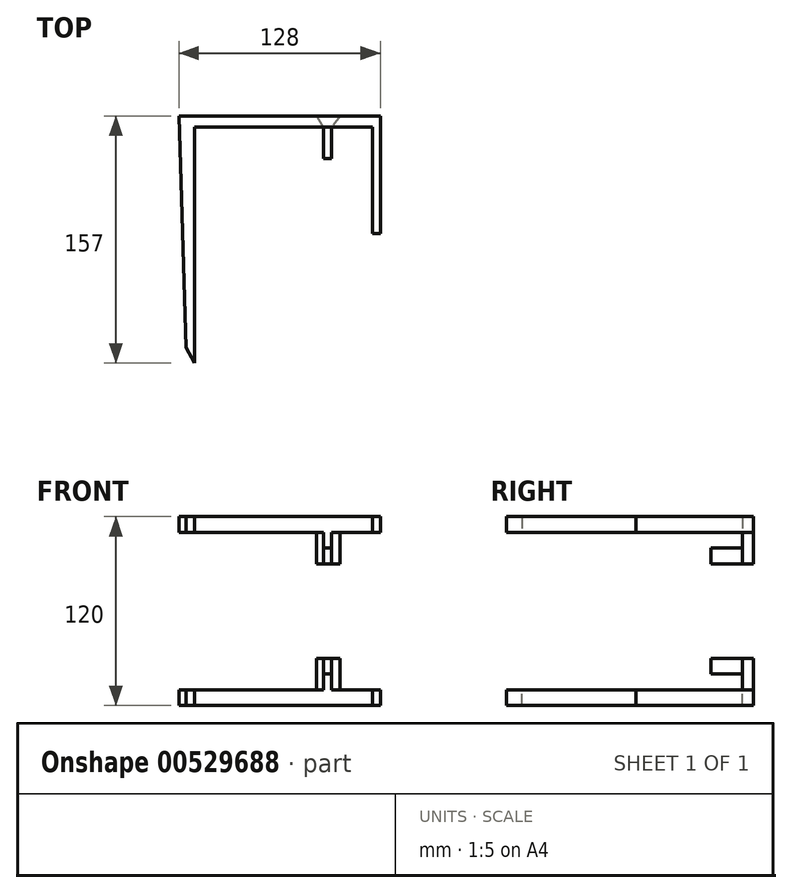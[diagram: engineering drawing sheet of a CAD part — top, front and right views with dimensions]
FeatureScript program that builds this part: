
annotation { "Feature Type Name" : "Feature", "Feature Type Description" : "" }
export const myFeature = defineFeature(function(context is Context, id is Id, definition is map)
    precondition{}
    {
        {
            var Q0;
            Q0=qCreatedBy(makeId("Top.planeOp"),FACE);
            var sketch = newSketch(context, id + "F0", { "sketchPlane" : qUnion([Q0])});
            skLineSegment(sketch, "E0", {"start": v(-97.85, -80.95) * mm, "end": v(-92.49, -90.95) * mm});
            skLineSegment(sketch, "E1", {"start": v(-92.49, -90.95) * mm, "end": v(-92.49, 59.05) * mm});
            skLineSegment(sketch, "E2", {"start": v(-92.49, 59.05) * mm, "end": v(20.51, 59.05) * mm});
            skLineSegment(sketch, "E3", {"start": v(20.51, 59.05) * mm, "end": v(20.51, -8.55) * mm});
            skLineSegment(sketch, "E4", {"start": v(20.51, -8.55) * mm, "end": v(25.51, -8.55) * mm});
            skLineSegment(sketch, "E5", {"start": v(25.51, -8.55) * mm, "end": v(25.51, 66.05) * mm});
            skLineSegment(sketch, "E6", {"start": v(25.51, 66.05) * mm, "end": v(-102.49, 66.05) * mm});
            skLineSegment(sketch, "E7", {"start": v(-102.49, 66.05) * mm, "end": v(-97.85, -80.95) * mm});
            skLineSegment(sketch, "E8.bottom", {"start": v(-10.49, 59.05) * mm, "end": v(-5.49, 59.05) * mm});
            skLineSegment(sketch, "E9", {"start": v(-16.3, 66.05) * mm, "end": v(0, 66.05) * mm});
            skSolve(sketch);
        }
        {
            var Q0;
            Q0=makeQuery(id+"F0.imprint","IMPRINT",FACE,{"disambiguationData":[TD([[makeQuery(id+"F0.imprint","IMPRINT",EDGE,{"derivedFrom":sQuery(id+"F0.wireOp",EDGE,"E0")}),1.0]])]});
            var Q1;
            {var subQ2=sQuery(id+"F0.wireOp",EDGE,"E3");Q1=makeQuery(id+"F0.imprint","IMPRINT",FACE,{"disambiguationData":[TD([[makeQuery(id+"F0.imprint","IMPRINT",EDGE,{"derivedFrom":subQ2}),1.0]])]});}
            var Q2;
            Q2=makeQuery(id+"F0.imprint","IMPRINT",FACE,{"disambiguationData":[TD([[makeQuery(id+"F0.imprint","IMPRINT",EDGE,{"derivedFrom":sQuery(id+"F0.wireOp",EDGE,"E8.bottom")}),1.0]])]});
            var Q3;
            Q3=sQuery(id+"F0.wireOp",EDGE,"E7");
            var Q4;
            Q4=sQuery(id+"F0.wireOp",EDGE,"E0");
            var Q5;
            Q5=sQuery(id+"F0.wireOp",EDGE,"E1");
            var Q6;
            Q6=sQuery(id+"F0.wireOp",EDGE,"E6");
            extrude(context, id + "F1", {"entities" : qUnion([Q0, Q1, Q2]), "surfaceEntities" : qUnion([Q3, Q4, Q5, Q6]), "oppositeDirection" : true, "depth" : 10 * mm});
        }
        {
            var Q0;
            Q0=makeQuery(id+"F1.opExtrude","CAP_FACE",FACE,{"disambiguationData":[OSD([sQuery(id+"F0.wireOp",EDGE,"E0"),sQuery(id+"F0.wireOp",EDGE,"E1"),sQuery(id+"F0.wireOp",EDGE,"E2"),sQuery(id+"F0.wireOp",EDGE,"E3"),sQuery(id+"F0.wireOp",EDGE,"E4"),sQuery(id+"F0.wireOp",EDGE,"E5"),sQuery(id+"F0.wireOp",EDGE,"E6"),sQuery(id+"F0.wireOp",EDGE,"E7"),sQuery(id+"F0.wireOp",EDGE,"E8.bottom"),sQuery(id+"F0.wireOp",EDGE,"E9")])],"isStart":true});
            var sketch = newSketch(context, id + "F2", { "sketchPlane" : qUnion([Q0])});
            skLineSegment(sketch, "E10", {"start": v(-5.49, 59.05) * mm, "end": v(-5.49, 29.05) * mm});
            skLineSegment(sketch, "E11", {"start": v(-5.49, 29.05) * mm, "end": v(-10.49, 29.05) * mm});
            skLineSegment(sketch, "E12", {"start": v(-10.49, 29.05) * mm, "end": v(-10.49, 59.05) * mm});
            skLineSegment(sketch, "E13", {"start": v(-10.49, 59.05) * mm, "end": v(-15, 66.05) * mm});
            skLineSegment(sketch, "E14", {"start": v(-15, 66.05) * mm, "end": v(0, 66.05) * mm});
            skLineSegment(sketch, "E15", {"start": v(0, 66.05) * mm, "end": v(-5.49, 59.05) * mm});
            skSolve(sketch);
        }
        {
            var Q0;
            {var subQ0=sQuery(id+"F2.wireOp",EDGE,"E13");Q0=makeQuery(id+"F2.imprint","IMPRINT",FACE,{"disambiguationData":[TD([[makeQuery(id+"F2.imprint","IMPRINT",EDGE,{"derivedFrom":subQ0}),-1.0]])]});}
            extrude(context, id + "F3", {"entities" : qUnion([Q0]), "operationType" : NewBodyOperationType.ADD, "depth" : 20 * mm});
        }
        {
            var Q0;
            {var subQ0=sQuery(id+"F0.wireOp",EDGE,"E8.bottom");var subQ1=sQuery(id+"F0.wireOp",EDGE,"E2");Q0=makeQuery(id+"F3.boolean.opBoolean","MERGE",FACE,{"derivedFrom":[makeQuery(id+"F1.opExtrude","SWEPT_FACE",FACE,{"disambiguationData":[OSD([subQ1,subQ0])]}),makeQuery(id+"F3.opExtrude","SWEPT_FACE",FACE,{"disambiguationData":[OSD([subQ1,subQ0])]})]});}
            var sketch = newSketch(context, id + "F4", { "sketchPlane" : qUnion([Q0])});
            skLineSegment(sketch, "E16", {"start": v(-10.49, 10) * mm, "end": v(-5.49, 10) * mm});
            skLineSegment(sketch, "E17", {"start": v(-5.49, 10) * mm, "end": v(-5.49, 20) * mm});
            skLineSegment(sketch, "E18", {"start": v(-5.49, 20) * mm, "end": v(-10.49, 20) * mm});
            skLineSegment(sketch, "E19", {"start": v(-10.49, 20) * mm, "end": v(-10.49, 10) * mm});
            skSolve(sketch);
        }
        {
            var Q0;
            Q0=makeQuery(id+"F4.imprint","IMPRINT",FACE,{"disambiguationData":[TD([[makeQuery(id+"F4.imprint","IMPRINT",EDGE,{"derivedFrom":sQuery(id+"F4.wireOp",EDGE,"E16")}),1.0]])]});
            extrude(context, id + "F5", {"entities" : qUnion([Q0]), "operationType" : NewBodyOperationType.ADD, "depth" : 20 * mm});
        }
        {
            var Q0;
            Q0=makeQuery(id+"F1.opExtrude","SWEPT_BODY",BODY,{"disambiguationData":[OSD([sQuery(id+"F0.wireOp",EDGE,"E0"),sQuery(id+"F0.wireOp",EDGE,"E1"),sQuery(id+"F0.wireOp",EDGE,"E2"),sQuery(id+"F0.wireOp",EDGE,"E3"),sQuery(id+"F0.wireOp",EDGE,"E4"),sQuery(id+"F0.wireOp",EDGE,"E5"),sQuery(id+"F0.wireOp",EDGE,"E6"),sQuery(id+"F0.wireOp",EDGE,"E7"),sQuery(id+"F0.wireOp",EDGE,"E8.bottom"),sQuery(id+"F0.wireOp",EDGE,"E9")])]});
            transform(context, id + "F6", {"entities" : qUnion([Q0]), "transformType" : TransformType.TRANSLATION_3D, "dx" : 0 * mm, "dy" : 0 * mm, "dz" : -100 * mm, "makeCopy" : true});
        }
        {
            var Q0;
            Q0=makeQuery(id+"F6.opPattern","COPY",BODY,{"derivedFrom":makeQuery(id+"F1.opExtrude","SWEPT_BODY",BODY,{"disambiguationData":[OSD([sQuery(id+"F0.wireOp",EDGE,"E0"),sQuery(id+"F0.wireOp",EDGE,"E1"),sQuery(id+"F0.wireOp",EDGE,"E2"),sQuery(id+"F0.wireOp",EDGE,"E3"),sQuery(id+"F0.wireOp",EDGE,"E4"),sQuery(id+"F0.wireOp",EDGE,"E5"),sQuery(id+"F0.wireOp",EDGE,"E6"),sQuery(id+"F0.wireOp",EDGE,"E7"),sQuery(id+"F0.wireOp",EDGE,"E8.bottom"),sQuery(id+"F0.wireOp",EDGE,"E9")])]}),"instanceName":"1"});
            var Q1;
            Q1=qCreatedBy(makeId("Top.planeOp"),FACE);
            mirror(context, id + "F7", {"entities" : qUnion([Q0]), "mirrorPlane" : qUnion([Q1])});
        }
        {
            var Q0;
            Q0=makeQuery(id+"F6.opPattern","COPY",BODY,{"derivedFrom":makeQuery(id+"F1.opExtrude","SWEPT_BODY",BODY,{"disambiguationData":[OSD([sQuery(id+"F0.wireOp",EDGE,"E0"),sQuery(id+"F0.wireOp",EDGE,"E1"),sQuery(id+"F0.wireOp",EDGE,"E2"),sQuery(id+"F0.wireOp",EDGE,"E3"),sQuery(id+"F0.wireOp",EDGE,"E4"),sQuery(id+"F0.wireOp",EDGE,"E5"),sQuery(id+"F0.wireOp",EDGE,"E6"),sQuery(id+"F0.wireOp",EDGE,"E7"),sQuery(id+"F0.wireOp",EDGE,"E8.bottom"),sQuery(id+"F0.wireOp",EDGE,"E9")])]}),"instanceName":"1"});
            deleteBodies(context, id + "F8", {"entities" : qUnion([Q0])});
        }
    });
